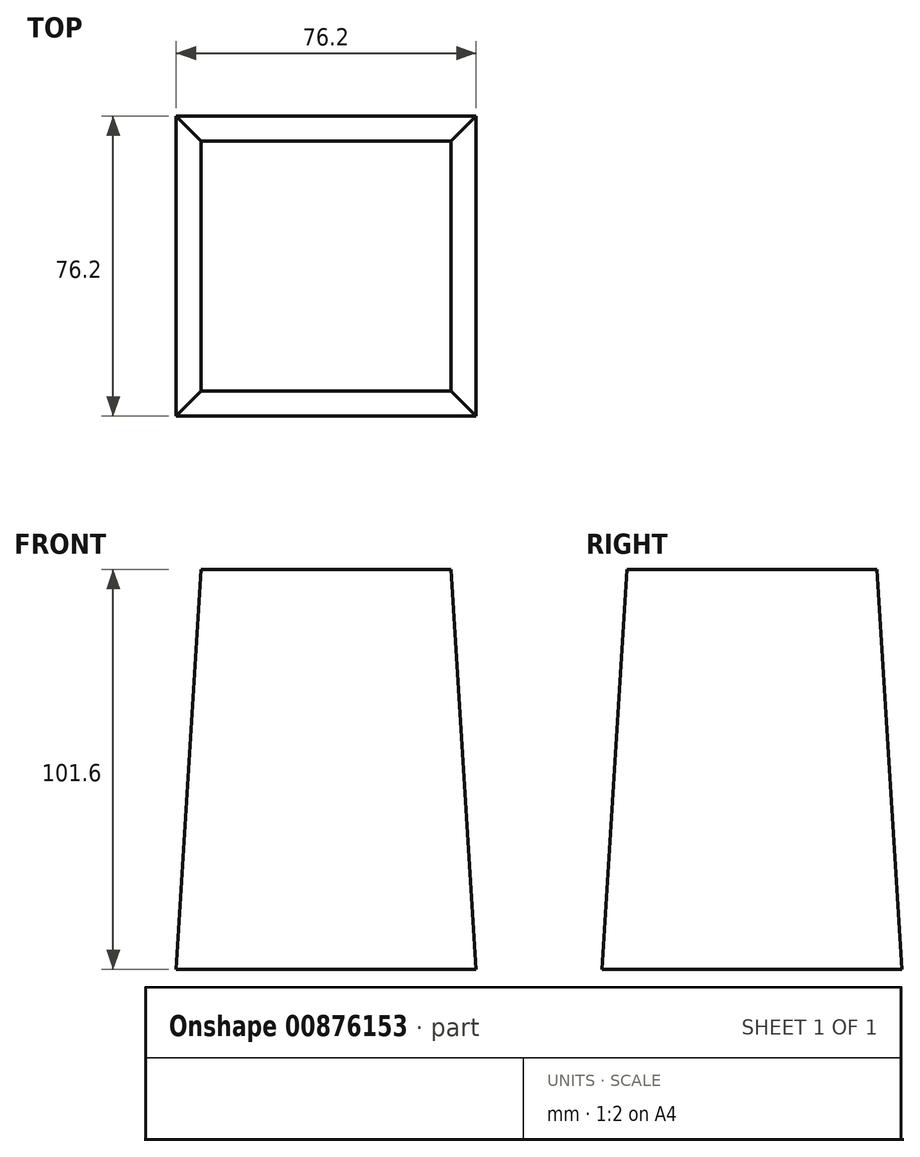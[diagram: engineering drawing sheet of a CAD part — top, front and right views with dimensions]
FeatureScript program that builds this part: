
annotation { "Feature Type Name" : "Feature", "Feature Type Description" : "" }
export const myFeature = defineFeature(function(context is Context, id is Id, definition is map)
    precondition{}
    {
        {
            var Q0;
            Q0=qCreatedBy(makeId("Top.planeOp"),FACE);
            var sketch = newSketch(context, id + "F0", { "sketchPlane" : qUnion([Q0])});
            skLineSegment(sketch, "E0", {"start": v(0, 0) * mm, "end": v(0, 76.2) * mm});
            skLineSegment(sketch, "E1", {"start": v(0, 76.2) * mm, "end": v(-76.2, 76.2) * mm});
            skLineSegment(sketch, "E2", {"start": v(-76.2, 76.2) * mm, "end": v(-76.2, 0) * mm});
            skLineSegment(sketch, "E3", {"start": v(-76.2, 0) * mm, "end": v(0, 0) * mm});
            skSolve(sketch);
        }
        {
            var Q0;
            Q0=makeQuery(id+"F0.imprint","IMPRINT",FACE,{"disambiguationData":[TD([[makeQuery(id+"F0.imprint","IMPRINT",EDGE,{"derivedFrom":sQuery(id+"F0.wireOp",EDGE,"E0")}),1.0]])]});
            extrude(context, id + "F1", {"entities" : qUnion([Q0]), "depth" : 101.6 * mm, "offsetDistance" : 25.4 * mm});
        }
        {
            var Q0;
            Q0=makeQuery(id+"F1.opExtrude","CAP_EDGE",EDGE,{"disambiguationData":[OSD([sQuery(id+"F0.wireOp",EDGE,"E3")])],"isStart":false});
            var Q1;
            Q1=makeQuery(id+"F1.opExtrude","CAP_EDGE",EDGE,{"disambiguationData":[OSD([sQuery(id+"F0.wireOp",EDGE,"E2")])],"isStart":false});
            var Q2;
            Q2=makeQuery(id+"F1.opExtrude","CAP_EDGE",EDGE,{"disambiguationData":[OSD([sQuery(id+"F0.wireOp",EDGE,"E0")])],"isStart":false});
            var Q3;
            Q3=makeQuery(id+"F1.opExtrude","CAP_EDGE",EDGE,{"disambiguationData":[OSD([sQuery(id+"F0.wireOp",EDGE,"E1")])],"isStart":false});
            chamfer(context, id + "F2", {"entities" : qUnion([Q0, Q1, Q2, Q3]), "chamferType" : ChamferType.TWO_OFFSETS, "width1" : 6.35 * mm, "oppositeDirection" : false, "width2" : 101.6 * mm, "tangentPropagation" : true});
        }
    });
